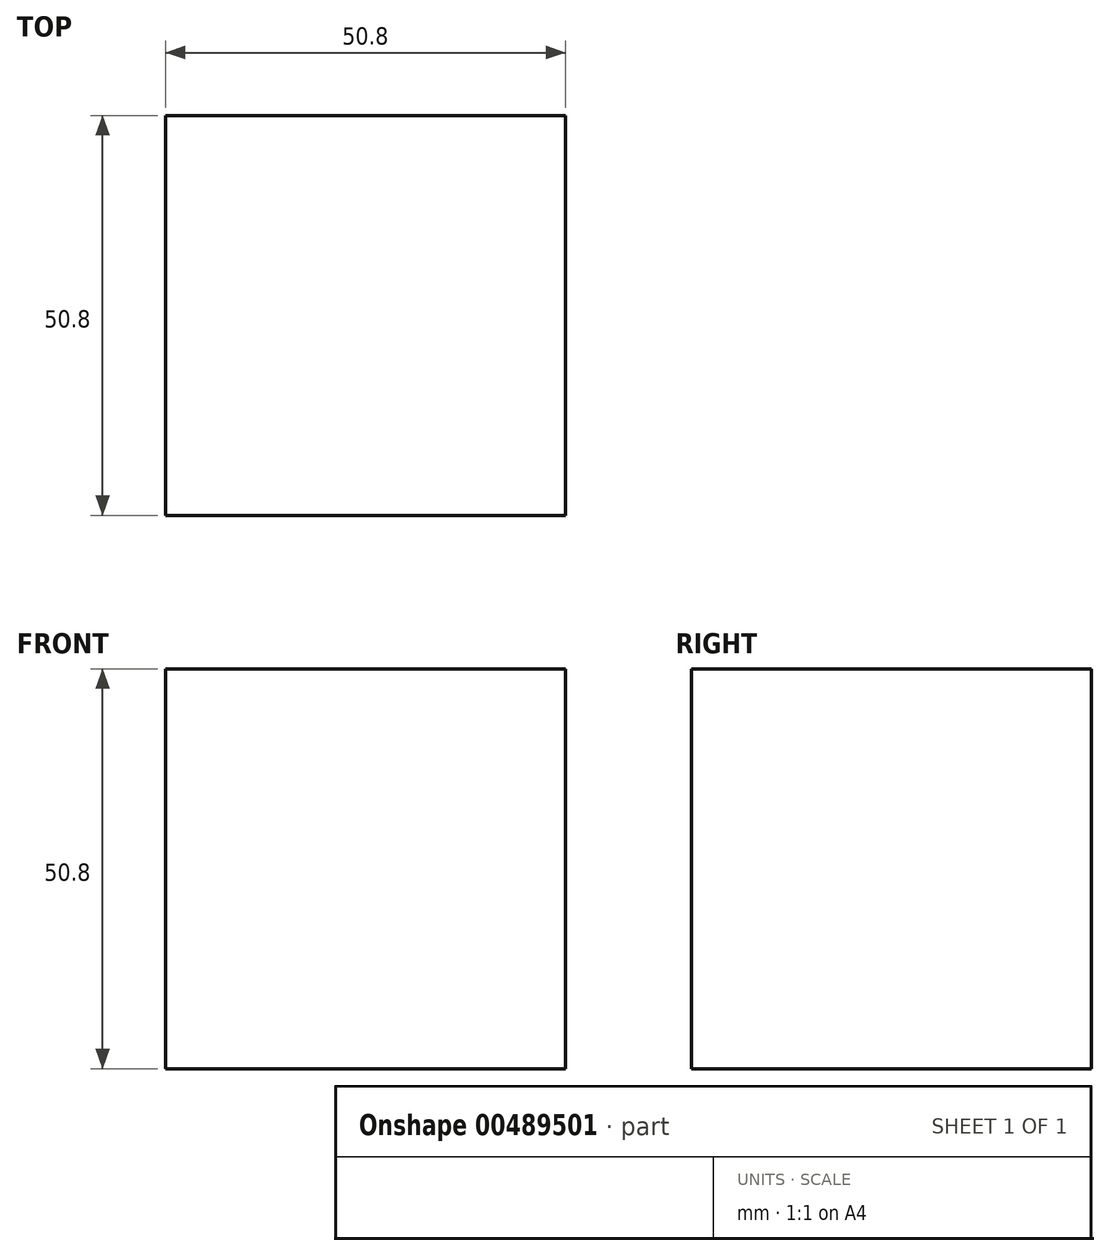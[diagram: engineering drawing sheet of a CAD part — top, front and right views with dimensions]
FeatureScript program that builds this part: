
annotation { "Feature Type Name" : "Feature", "Feature Type Description" : "" }
export const myFeature = defineFeature(function(context is Context, id is Id, definition is map)
    precondition{}
    {
        {
            var Q0;
            Q0=qCreatedBy(makeId("Right.planeOp"),FACE);
            var sketch = newSketch(context, id + "F0", { "sketchPlane" : qUnion([Q0])});
            skLineSegment(sketch, "E0", {"start": v(0, -3.02) * mm, "end": v(0, 0) * mm});
            skLineSegment(sketch, "E1", {"start": v(0, 0) * mm, "end": v(50.8, 0) * mm});
            skLineSegment(sketch, "E2", {"start": v(50.8, 0) * mm, "end": v(50.8, 50.8) * mm});
            skLineSegment(sketch, "E3", {"start": v(50.8, 50.8) * mm, "end": v(0, 50.8) * mm});
            skLineSegment(sketch, "E4", {"start": v(0, 50.8) * mm, "end": v(0, 0) * mm});
            skSolve(sketch);
        }
        {
            var Q0;
            Q0 = qSketchRegion(id + "F0", true);
            extrude(context, id + "F1", {"entities" : qUnion([Q0]), "depth" : 50.8 * mm});
        }
        {
            var Q0;
            Q0=qCreatedBy(makeId("Front.planeOp"),FACE);
            var sketch = newSketch(context, id + "F2", { "sketchPlane" : qUnion([Q0])});
            skCircle(sketch, "E5", {"center": v(25.35, 25.57) * mm, "radius": 12.7 * mm});
            skSolve(sketch);
        }
        {
            var Q0;
            Q0 = qSketchRegion(id + "F2", true);
            extrude(context, id + "F3", {"entities" : qUnion([Q0]), "operationType" : NewBodyOperationType.REMOVE, "oppositeDirection" : true, "depth" : 50.8 * mm});
        }
        {
            var Q0;
            Q0 = qSketchRegion(id + "F0", true);
            extrude(context, id + "F4", {"entities" : qUnion([Q0]), "operationType" : NewBodyOperationType.ADD, "depth" : 50.8 * mm});
        }
    });
